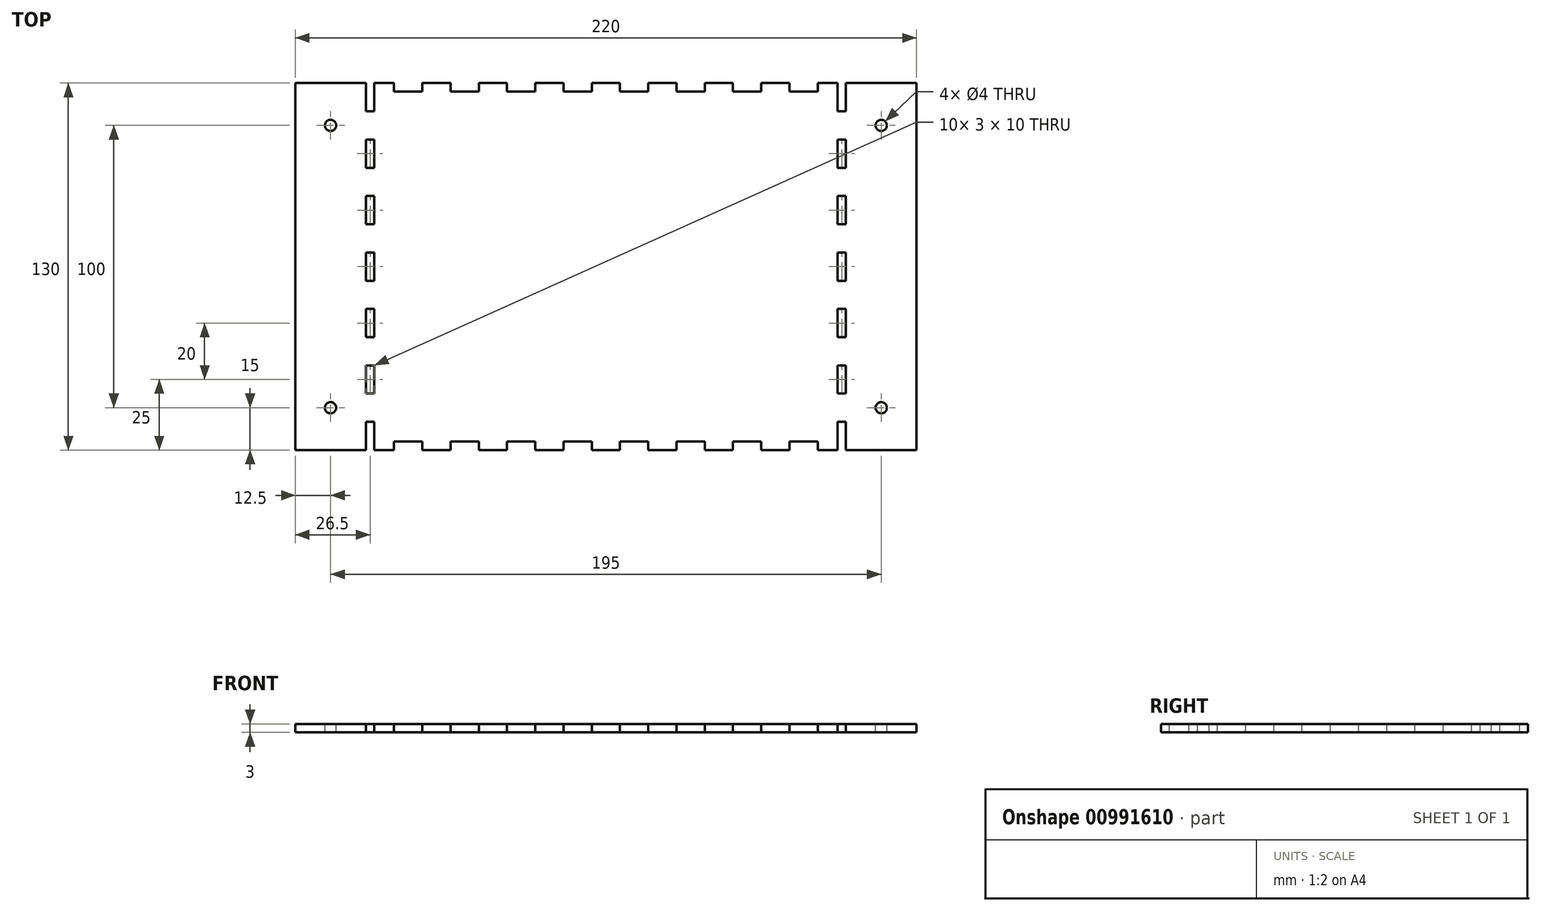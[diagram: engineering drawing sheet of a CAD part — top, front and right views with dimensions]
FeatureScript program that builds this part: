
annotation { "Feature Type Name" : "Feature", "Feature Type Description" : "" }
export const myFeature = defineFeature(function(context is Context, id is Id, definition is map)
    precondition{}
    {
        {
            var Q0;
            Q0=qCreatedBy(makeId("Top.planeOp"),FACE);
            var sketch = newSketch(context, id + "F0", { "sketchPlane" : qUnion([Q0])});
            skLineSegment(sketch, "E0.bottom", {"start": v(110, -65) * mm, "end": v(-110, -65) * mm});
            skLineSegment(sketch, "E0.top", {"start": v(110, 65) * mm, "end": v(-110, 65) * mm});
            skLineSegment(sketch, "E0.left", {"start": v(110, -65) * mm, "end": v(110, 65) * mm});
            skLineSegment(sketch, "E0.right", {"start": v(-110, -65) * mm, "end": v(-110, 65) * mm});
            skPoint(sketch, "E0.middle", {"position": v(0, 0) * mm});
            skSolve(sketch);
        }
        {
            var Q0;
            Q0=qSketchRegion(id+"F0",true);
            extrude(context, id + "F1", {"entities" : qUnion([Q0]), "depth" : 3 * mm, "offsetDistance" : 25 * mm});
        }
        {
            var Q0;
            Q0=makeQuery(id+"F1.opExtrude","CAP_FACE",FACE,{"disambiguationData":[OSD([sQuery(id+"F0.wireOp",EDGE,"E0.bottom"),sQuery(id+"F0.wireOp",EDGE,"E0.top"),sQuery(id+"F0.wireOp",EDGE,"E0.left"),sQuery(id+"F0.wireOp",EDGE,"E0.right")])],"isStart":false});
            var sketch = newSketch(context, id + "F2", { "sketchPlane" : qUnion([Q0])});
            skLineSegment(sketch, "E1.bottom", {"start": v(-75, -65) * mm, "end": v(-65, -65) * mm});
            skLineSegment(sketch, "E1.top", {"start": v(-75, -62) * mm, "end": v(-65, -62) * mm});
            skLineSegment(sketch, "E1.right", {"start": v(-65, -65) * mm, "end": v(-65, -62) * mm});
            skLineSegment(sketch, "E2.1.0.0", {"start": v(-55, -65) * mm, "end": v(-45, -65) * mm});
            skLineSegment(sketch, "E2.1.0.1", {"start": v(-55, -62) * mm, "end": v(-45, -62) * mm});
            skLineSegment(sketch, "E2.1.0.2", {"start": v(-55, -65) * mm, "end": v(-55, -62) * mm});
            skLineSegment(sketch, "E2.1.0.3", {"start": v(-45, -65) * mm, "end": v(-45, -62) * mm});
            skLineSegment(sketch, "E2.2.0.0", {"start": v(-35, -65) * mm, "end": v(-25, -65) * mm});
            skLineSegment(sketch, "E2.2.0.1", {"start": v(-35, -62) * mm, "end": v(-25, -62) * mm});
            skLineSegment(sketch, "E2.2.0.2", {"start": v(-35, -65) * mm, "end": v(-35, -62) * mm});
            skLineSegment(sketch, "E2.2.0.3", {"start": v(-25, -65) * mm, "end": v(-25, -62) * mm});
            skLineSegment(sketch, "E2.3.0.0", {"start": v(-15, -65) * mm, "end": v(-5, -65) * mm});
            skLineSegment(sketch, "E2.3.0.1", {"start": v(-15, -62) * mm, "end": v(-5, -62) * mm});
            skLineSegment(sketch, "E2.3.0.2", {"start": v(-15, -65) * mm, "end": v(-15, -62) * mm});
            skLineSegment(sketch, "E2.3.0.3", {"start": v(-5, -65) * mm, "end": v(-5, -62) * mm});
            skLineSegment(sketch, "E2.4.0.0", {"start": v(5, -65) * mm, "end": v(15, -65) * mm});
            skLineSegment(sketch, "E2.4.0.1", {"start": v(5, -62) * mm, "end": v(15, -62) * mm});
            skLineSegment(sketch, "E2.4.0.2", {"start": v(5, -65) * mm, "end": v(5, -62) * mm});
            skLineSegment(sketch, "E2.4.0.3", {"start": v(15, -65) * mm, "end": v(15, -62) * mm});
            skLineSegment(sketch, "E2.5.0.0", {"start": v(25, -65) * mm, "end": v(35, -65) * mm});
            skLineSegment(sketch, "E2.5.0.1", {"start": v(25, -62) * mm, "end": v(35, -62) * mm});
            skLineSegment(sketch, "E2.5.0.2", {"start": v(25, -65) * mm, "end": v(25, -62) * mm});
            skLineSegment(sketch, "E2.5.0.3", {"start": v(35, -65) * mm, "end": v(35, -62) * mm});
            skLineSegment(sketch, "E2.6.0.0", {"start": v(45, -65) * mm, "end": v(55, -65) * mm});
            skLineSegment(sketch, "E2.6.0.1", {"start": v(45, -62) * mm, "end": v(55, -62) * mm});
            skLineSegment(sketch, "E2.6.0.2", {"start": v(45, -65) * mm, "end": v(45, -62) * mm});
            skLineSegment(sketch, "E2.6.0.3", {"start": v(55, -65) * mm, "end": v(55, -62) * mm});
            skLineSegment(sketch, "E2.7.0.0", {"start": v(65, -65) * mm, "end": v(75, -65) * mm});
            skLineSegment(sketch, "E2.7.0.1", {"start": v(65, -62) * mm, "end": v(75, -62) * mm});
            skLineSegment(sketch, "E2.7.0.2", {"start": v(65, -65) * mm, "end": v(65, -62) * mm});
            skLineSegment(sketch, "E2.7.0.3", {"start": v(75, -65) * mm, "end": v(75, -62) * mm});
            skLineSegment(sketch, "E2.direction1", {"start": v(-75, -65) * mm, "end": v(-55, -65) * mm, "construction": true});
            skLineSegment(sketch, "E3.direction1", {"start": v(-75, -65) * mm, "end": v(-50, -65) * mm, "construction": true});
            skLineSegment(sketch, "E4", {"start": v(-75, -62) * mm, "end": v(-75, -65) * mm});
            skLineSegment(sketch, "E5.bottom", {"start": v(-85, -65) * mm, "end": v(-82, -65) * mm});
            skLineSegment(sketch, "E5.top", {"start": v(-85, -55) * mm, "end": v(-82, -55) * mm});
            skLineSegment(sketch, "E5.left", {"start": v(-85, -65) * mm, "end": v(-85, -55) * mm});
            skLineSegment(sketch, "E5.right", {"start": v(-82, -65) * mm, "end": v(-82, -55) * mm});
            skLineSegment(sketch, "E6.0.1.0", {"start": v(-85, -45) * mm, "end": v(-85, -35) * mm});
            skLineSegment(sketch, "E6.0.1.1", {"start": v(-82, -45) * mm, "end": v(-82, -35) * mm});
            skLineSegment(sketch, "E6.0.1.2", {"start": v(-85, -35) * mm, "end": v(-82, -35) * mm});
            skLineSegment(sketch, "E6.0.1.3", {"start": v(-85, -45) * mm, "end": v(-82, -45) * mm});
            skLineSegment(sketch, "E6.0.2.0", {"start": v(-85, -25) * mm, "end": v(-85, -15) * mm});
            skLineSegment(sketch, "E6.0.2.1", {"start": v(-82, -25) * mm, "end": v(-82, -15) * mm});
            skLineSegment(sketch, "E6.0.2.2", {"start": v(-85, -15) * mm, "end": v(-82, -15) * mm});
            skLineSegment(sketch, "E6.0.2.3", {"start": v(-85, -25) * mm, "end": v(-82, -25) * mm});
            skLineSegment(sketch, "E6.0.3.0", {"start": v(-85, -5) * mm, "end": v(-85, 5) * mm});
            skLineSegment(sketch, "E6.0.3.1", {"start": v(-82, -5) * mm, "end": v(-82, 5) * mm});
            skLineSegment(sketch, "E6.0.3.2", {"start": v(-85, 5) * mm, "end": v(-82, 5) * mm});
            skLineSegment(sketch, "E6.0.3.3", {"start": v(-85, -5) * mm, "end": v(-82, -5) * mm});
            skLineSegment(sketch, "E6.0.4.0", {"start": v(-85, 15) * mm, "end": v(-85, 25) * mm});
            skLineSegment(sketch, "E6.0.4.1", {"start": v(-82, 15) * mm, "end": v(-82, 25) * mm});
            skLineSegment(sketch, "E6.0.4.2", {"start": v(-85, 25) * mm, "end": v(-82, 25) * mm});
            skLineSegment(sketch, "E6.0.4.3", {"start": v(-85, 15) * mm, "end": v(-82, 15) * mm});
            skLineSegment(sketch, "E6.0.5.0", {"start": v(-85, 35) * mm, "end": v(-85, 45) * mm});
            skLineSegment(sketch, "E6.0.5.1", {"start": v(-82, 35) * mm, "end": v(-82, 45) * mm});
            skLineSegment(sketch, "E6.0.5.2", {"start": v(-85, 45) * mm, "end": v(-82, 45) * mm});
            skLineSegment(sketch, "E6.0.5.3", {"start": v(-85, 35) * mm, "end": v(-82, 35) * mm});
            skLineSegment(sketch, "E6.0.6.0", {"start": v(-85, 55) * mm, "end": v(-85, 65) * mm});
            skLineSegment(sketch, "E6.0.6.1", {"start": v(-82, 55) * mm, "end": v(-82, 65) * mm});
            skLineSegment(sketch, "E6.0.6.2", {"start": v(-85, 65) * mm, "end": v(-82, 65) * mm});
            skLineSegment(sketch, "E6.0.6.3", {"start": v(-85, 55) * mm, "end": v(-82, 55) * mm});
            skLineSegment(sketch, "E6.direction1", {"start": v(-85, -65) * mm, "end": v(-60, -65) * mm, "construction": true});
            skLineSegment(sketch, "E6.direction2", {"start": v(-85, -65) * mm, "end": v(-85, -45) * mm, "construction": true});
            skLineSegment(sketch, "E7", {"start": v(-110, 0) * mm, "end": v(110, 0) * mm, "construction": true});
            skLineSegment(sketch, "E8.MirrorCS", {"start": v(-45, 65) * mm, "end": v(-45, 62) * mm});
            skLineSegment(sketch, "E9.MirrorCS", {"start": v(25, 65) * mm, "end": v(25, 62) * mm});
            skLineSegment(sketch, "E10.MirrorCS", {"start": v(-75, 62) * mm, "end": v(-75, 65) * mm});
            skLineSegment(sketch, "E11.MirrorCS", {"start": v(65, 65) * mm, "end": v(65, 62) * mm});
            skLineSegment(sketch, "E12.MirrorCS", {"start": v(-15, 65) * mm, "end": v(-15, 62) * mm});
            skLineSegment(sketch, "E13.MirrorCS", {"start": v(-75, 65) * mm, "end": v(-65, 65) * mm});
            skLineSegment(sketch, "E14.MirrorCS", {"start": v(-25, 65) * mm, "end": v(-25, 62) * mm});
            skLineSegment(sketch, "E15.MirrorCS", {"start": v(-55, 65) * mm, "end": v(-55, 62) * mm});
            skLineSegment(sketch, "E16.MirrorCS", {"start": v(-65, 65) * mm, "end": v(-65, 62) * mm});
            skLineSegment(sketch, "E17.MirrorCS", {"start": v(75, 65) * mm, "end": v(75, 62) * mm});
            skLineSegment(sketch, "E18.MirrorCS", {"start": v(-5, 65) * mm, "end": v(-5, 62) * mm});
            skLineSegment(sketch, "E19.MirrorCS", {"start": v(55, 65) * mm, "end": v(55, 62) * mm});
            skLineSegment(sketch, "E20.MirrorCS", {"start": v(45, 65) * mm, "end": v(45, 62) * mm});
            skLineSegment(sketch, "E21.MirrorCS", {"start": v(5, 65) * mm, "end": v(5, 62) * mm});
            skLineSegment(sketch, "E22.MirrorCS", {"start": v(15, 65) * mm, "end": v(15, 62) * mm});
            skLineSegment(sketch, "E23.MirrorCS", {"start": v(-35, 65) * mm, "end": v(-35, 62) * mm});
            skLineSegment(sketch, "E24.MirrorCS", {"start": v(35, 65) * mm, "end": v(35, 62) * mm});
            skLineSegment(sketch, "E25.MirrorCS", {"start": v(-75, 65) * mm, "end": v(-55, 65) * mm, "construction": true});
            skLineSegment(sketch, "E26.MirrorCS", {"start": v(-55, 65) * mm, "end": v(-45, 65) * mm});
            skLineSegment(sketch, "E27.MirrorCS", {"start": v(25, 62) * mm, "end": v(35, 62) * mm});
            skLineSegment(sketch, "E28.MirrorCS", {"start": v(-35, 62) * mm, "end": v(-25, 62) * mm});
            skLineSegment(sketch, "E29.MirrorCS", {"start": v(-35, 65) * mm, "end": v(-25, 65) * mm});
            skLineSegment(sketch, "E30.MirrorCS", {"start": v(25, 65) * mm, "end": v(35, 65) * mm});
            skLineSegment(sketch, "E31.MirrorCS", {"start": v(-15, 62) * mm, "end": v(-5, 62) * mm});
            skLineSegment(sketch, "E32.MirrorCS", {"start": v(-75, 62) * mm, "end": v(-65, 62) * mm});
            skLineSegment(sketch, "E33.MirrorCS", {"start": v(-15, 65) * mm, "end": v(-5, 65) * mm});
            skLineSegment(sketch, "E34.MirrorCS", {"start": v(45, 65) * mm, "end": v(55, 65) * mm});
            skLineSegment(sketch, "E35.MirrorCS", {"start": v(-75, 65) * mm, "end": v(-50, 65) * mm, "construction": true});
            skLineSegment(sketch, "E36.MirrorCS", {"start": v(45, 62) * mm, "end": v(55, 62) * mm});
            skLineSegment(sketch, "E37.MirrorCS", {"start": v(-55, 62) * mm, "end": v(-45, 62) * mm});
            skLineSegment(sketch, "E38.MirrorCS", {"start": v(5, 65) * mm, "end": v(15, 65) * mm});
            skLineSegment(sketch, "E39.MirrorCS", {"start": v(65, 65) * mm, "end": v(75, 65) * mm});
            skLineSegment(sketch, "E40.MirrorCS", {"start": v(5, 62) * mm, "end": v(15, 62) * mm});
            skLineSegment(sketch, "E41.MirrorCS", {"start": v(65, 62) * mm, "end": v(75, 62) * mm});
            skLineSegment(sketch, "E42", {"start": v(0, 65) * mm, "end": v(0, -62) * mm, "construction": true});
            skLineSegment(sketch, "E43.MirrorCS", {"start": v(85, -45) * mm, "end": v(82, -45) * mm});
            skLineSegment(sketch, "E44.MirrorCS", {"start": v(85, -25) * mm, "end": v(82, -25) * mm});
            skLineSegment(sketch, "E45.MirrorCS", {"start": v(85, 35) * mm, "end": v(82, 35) * mm});
            skLineSegment(sketch, "E46.MirrorCS", {"start": v(85, 55) * mm, "end": v(82, 55) * mm});
            skLineSegment(sketch, "E47.MirrorCS", {"start": v(85, 45) * mm, "end": v(82, 45) * mm});
            skLineSegment(sketch, "E48.MirrorCS", {"start": v(85, 15) * mm, "end": v(82, 15) * mm});
            skLineSegment(sketch, "E49.MirrorCS", {"start": v(85, 65) * mm, "end": v(82, 65) * mm});
            skLineSegment(sketch, "E50.MirrorCS", {"start": v(85, -65) * mm, "end": v(82, -65) * mm});
            skLineSegment(sketch, "E51.MirrorCS", {"start": v(85, -5) * mm, "end": v(82, -5) * mm});
            skLineSegment(sketch, "E52.MirrorCS", {"start": v(85, -15) * mm, "end": v(82, -15) * mm});
            skLineSegment(sketch, "E53.MirrorCS", {"start": v(85, -55) * mm, "end": v(82, -55) * mm});
            skLineSegment(sketch, "E54.MirrorCS", {"start": v(85, 25) * mm, "end": v(82, 25) * mm});
            skLineSegment(sketch, "E55.MirrorCS", {"start": v(85, 5) * mm, "end": v(82, 5) * mm});
            skLineSegment(sketch, "E56.MirrorCS", {"start": v(85, -35) * mm, "end": v(82, -35) * mm});
            skLineSegment(sketch, "E57.MirrorCS", {"start": v(85, -65) * mm, "end": v(85, -55) * mm});
            skLineSegment(sketch, "E58.MirrorCS", {"start": v(85, 15) * mm, "end": v(85, 25) * mm});
            skLineSegment(sketch, "E59.MirrorCS", {"start": v(82, -45) * mm, "end": v(82, -35) * mm});
            skLineSegment(sketch, "E60.MirrorCS", {"start": v(82, -25) * mm, "end": v(82, -15) * mm});
            skLineSegment(sketch, "E61.MirrorCS", {"start": v(85, -5) * mm, "end": v(85, 5) * mm});
            skLineSegment(sketch, "E62.MirrorCS", {"start": v(82, -5) * mm, "end": v(82, 5) * mm});
            skLineSegment(sketch, "E63.MirrorCS", {"start": v(85, -65) * mm, "end": v(85, -45) * mm, "construction": true});
            skLineSegment(sketch, "E64.MirrorCS", {"start": v(85, -45) * mm, "end": v(85, -35) * mm});
            skLineSegment(sketch, "E65.MirrorCS", {"start": v(82, 15) * mm, "end": v(82, 25) * mm});
            skLineSegment(sketch, "E66.MirrorCS", {"start": v(82, -65) * mm, "end": v(82, -55) * mm});
            skLineSegment(sketch, "E67.MirrorCS", {"start": v(85, -25) * mm, "end": v(85, -15) * mm});
            skLineSegment(sketch, "E68.MirrorCS", {"start": v(82, 35) * mm, "end": v(82, 45) * mm});
            skLineSegment(sketch, "E69.MirrorCS", {"start": v(82, 55) * mm, "end": v(82, 65) * mm});
            skLineSegment(sketch, "E70.MirrorCS", {"start": v(85, 35) * mm, "end": v(85, 45) * mm});
            skLineSegment(sketch, "E71.MirrorCS", {"start": v(85, 55) * mm, "end": v(85, 65) * mm});
            skSolve(sketch);
        }
        {
            var Q0;
            Q0=qSketchRegion(id+"F2",true);
            extrude(context, id + "F3", {"entities" : qUnion([Q0]), "operationType" : NewBodyOperationType.REMOVE, "endBound" : BoundingType.THROUGH_ALL, "oppositeDirection" : true, "depth" : 25 * mm, "offsetDistance" : 25 * mm});
        }
        {
            var Q0;
            Q0=makeQuery(id+"F1.opExtrude","CAP_FACE",FACE,{"disambiguationData":[OSD([sQuery(id+"F0.wireOp",EDGE,"E0.bottom"),sQuery(id+"F0.wireOp",EDGE,"E0.top"),sQuery(id+"F0.wireOp",EDGE,"E0.left"),sQuery(id+"F0.wireOp",EDGE,"E0.right")])],"isStart":false});
            var sketch = newSketch(context, id + "F4", { "sketchPlane" : qUnion([Q0])});
            skLineSegment(sketch, "E72", {"start": v(97.5, 65) * mm, "end": v(97.5, -65) * mm, "construction": true});
            skCircle(sketch, "E73", {"center": v(97.5, 50) * mm, "radius": 2 * mm});
            skLineSegment(sketch, "E74", {"start": v(-110, 0) * mm, "end": v(110, 0) * mm, "construction": true});
            skCircle(sketch, "E75.MirrorC", {"center": v(97.5, -50) * mm, "radius": 2 * mm});
            skLineSegment(sketch, "E76", {"start": v(0, 65) * mm, "end": v(0, -65) * mm, "construction": true});
            skCircle(sketch, "E77.MirrorC", {"center": v(-97.5, 50) * mm, "radius": 2 * mm});
            skCircle(sketch, "E78.MirrorC", {"center": v(-97.5, -50) * mm, "radius": 2 * mm});
            skSolve(sketch);
        }
        {
            var Q0;
            Q0=qSketchRegion(id+"F4",true);
            extrude(context, id + "F5", {"entities" : qUnion([Q0]), "operationType" : NewBodyOperationType.REMOVE, "endBound" : BoundingType.THROUGH_ALL, "oppositeDirection" : true, "depth" : 25 * mm, "offsetDistance" : 25 * mm});
        }
    });
